# Revit family: Søjle - SE
name_source: partatom
category: Structural Columns
units: mm (PartAtom-declared; Revit-internal decimal feet)

## family parameters
Always export as geometry = No
Beam cutback in plan = From bounding box
Cut with Voids When Loaded = No
Material for Model Behavior = Other
OmniClass Number = 23.25.30.11.14.11
OmniClass Title = Columns
Section Shape = Not Defined
Shared = No
Show family pre-cut in plan views = Yes

## types (1)
- SE 48/48
    Affaset Top = No
    Antal Recesser Bund = 0
    Bredde = 480 mm  [stored 1.5748 ft]
    Chamfer = 10 mm  [stored 0.0328084 ft]
    Dybde = 480 mm  [stored 1.5748 ft]
    Manufacturer = CRH Concrete
    Model = SE
    Type Chamfer = Chamfer Top
    Type Non = Non
    Type Recess Array F/B = Recess Array : Front/Back
    Type Recess Array L/R = Recess Array : Left/Right
    Type Recess F/B = Recess : Front/Back
    Type Recess L/R = Recess : Left/Right

note: [stored X ft] marks values corroborated as IEEE doubles in the binary element streams (Revit-internal decimal feet)

## geometry (parser evidence)
native form markers: Blend x2, Sweep x13
no freeform markers — native parametric forms only
